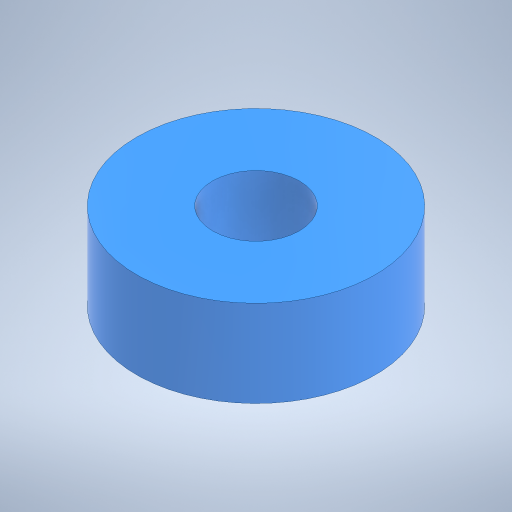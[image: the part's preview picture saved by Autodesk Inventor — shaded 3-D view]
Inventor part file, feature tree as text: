
AUTODESK INVENTOR PART (.ipt)
format: ipt  version: 2024 (Build 280153000, 153)  size: 216,576 bytes
history: native  units: in
note: dims shown in document units (in); Inventor stores cm internally (conversion verified against a paired STEP export)
features: extrude x1, sketch x1
ambient origin geometry x8: Origin, YZ Plane, XZ Plane, XY Plane, X Axis, Y Axis, Z Axis, Center Point
bodies: Solid1 (feature_tree)
feature tree (2):
  extrude  "Extrusion1"  Depth=0.25in
  sketch  "Sketch1"  dims[d0=0.6875in d1=0.25in d2=0.25in d3=0.0in]
